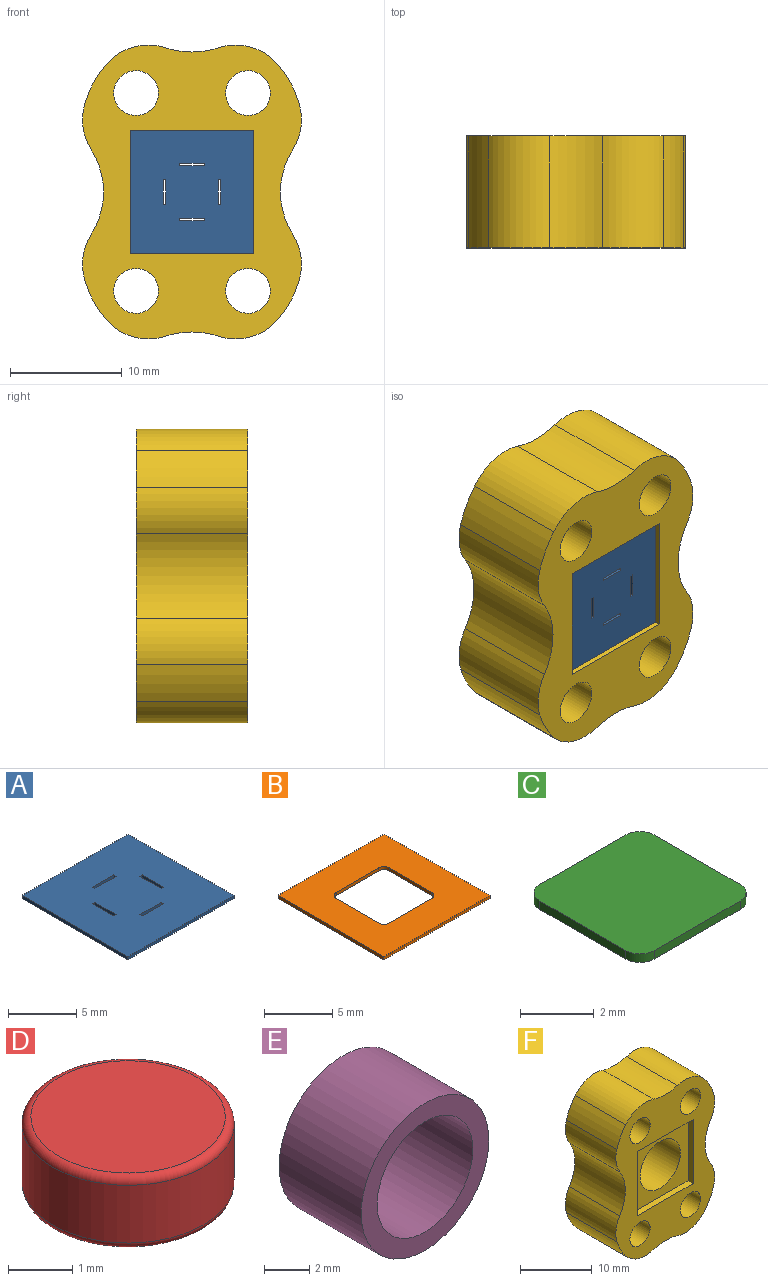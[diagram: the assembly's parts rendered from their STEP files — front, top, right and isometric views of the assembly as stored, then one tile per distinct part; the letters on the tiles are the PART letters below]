
ASSEMBLY  parts=6 mates=13
PART A: 22 faces, bbox 11x11x0.3 mm
  f0: plane 11x11mm, normal (0,0,1), area 118.8mm2, adj f2,f3,f4,f5,f6,f7,f8,f9
  f1: plane 11x11mm, normal (0,0,-1), area 118.8mm2, adj f2,f3,f4,f5,f6,f7,f8,f9
  f2: plane 11x0.28mm, normal (-1,0,0), area 3mm2, adj f0,f1,f3,f5
  f3: plane 11x0.28mm, normal (0,-1,0), area 3mm2, adj f0,f1,f2,f4
  f4: plane 11x0.28mm, normal (1,0,0), area 3mm2, adj f0,f1,f3,f5
  f5: plane 11x0.28mm, normal (0,1,0), area 3mm2, adj f0,f1,f2,f4
  f6: plane 0.28x0.25mm, normal (0,1,0), area 0.1mm2, adj f0,f1,f7,f8
  f7: plane 2.2x0.28mm, normal (1,0,0), area 0.6mm2, adj f0,f1,f6,f9
  f8: plane 2.2x0.28mm, normal (-1,0,0), area 0.6mm2, adj f0,f1,f6,f9
  f9: plane 0.28x0.25mm, normal (0,-1,0), area 0.1mm2, adj f0,f1,f7,f8
  f10: plane 2.2x0.28mm, normal (-1,0,0), area 0.6mm2, adj f0,f1,f11,f12
  f11: plane 0.28x0.25mm, normal (0,1,0), area 0.1mm2, adj f0,f1,f10,f13
  f12: plane 0.28x0.25mm, normal (0,-1,0), area 0.1mm2, adj f0,f1,f10,f13
  f13: plane 2.2x0.28mm, normal (1,0,0), area 0.6mm2, adj f0,f1,f11,f12
  f14: plane 0.28x0.25mm, normal (-1,0,0), area 0.1mm2, adj f0,f1,f15,f17
  f15: plane 2.2x0.28mm, normal (0,-1,0), area 0.6mm2, adj f0,f1,f14,f16
  f16: plane 0.28x0.25mm, normal (1,0,0), area 0.1mm2, adj f0,f1,f15,f17
  f17: plane 2.2x0.28mm, normal (0,1,0), area 0.6mm2, adj f0,f1,f14,f16
  f18: plane 2.2x0.28mm, normal (0,1,0), area 0.6mm2, adj f0,f1,f19,f20
  f19: plane 0.28x0.25mm, normal (1,0,0), area 0.1mm2, adj f0,f1,f18,f21
  f20: plane 0.28x0.25mm, normal (-1,0,0), area 0.1mm2, adj f0,f1,f18,f21
  f21: plane 2.2x0.28mm, normal (0,-1,0), area 0.6mm2, adj f0,f1,f19,f20
PART B: 14 faces, bbox 11x11x0.3 mm
  f0: plane 11x11mm, normal (0,0,-1), area 91mm2, adj f2,f3,f4,f5,f6,f7,f8,f9
  f1: plane 11x11mm, normal (0,0,1), area 91mm2, adj f2,f3,f4,f5,f6,f7,f8,f9
  f2: plane 11x0.28mm, normal (0,1,0), area 3.1mm2, adj f0,f1,f4,f5
  f3: plane 11x0.28mm, normal (0,-1,0), area 3.1mm2, adj f0,f1,f4,f5
  f4: plane 11x0.28mm, normal (1,0,0), area 3.1mm2, adj f0,f1,f2,f3
  f5: plane 11x0.28mm, normal (-1,0,0), area 3.1mm2, adj f0,f1,f2,f3
  f6: cylinder r=0.55mm len=0.55mm, axis (0,0,1), area 0.2mm2, adj f0,f1,f7,f13
  f7: plane 4.4x0.28mm, normal (-1,0,0), area 1.2mm2, adj f0,f1,f6,f8
  f8: cylinder r=0.55mm len=0.55mm, axis (0,0,1), area 0.2mm2, adj f0,f1,f7,f9
  f9: plane 4.4x0.28mm, normal (0,1,0), area 1.2mm2, adj f0,f1,f8,f10
  f10: cylinder r=0.55mm len=0.55mm, axis (0,0,1), area 0.2mm2, adj f0,f1,f9,f11
  f11: plane 4.4x0.28mm, normal (1,0,0), area 1.2mm2, adj f0,f1,f10,f12
  f12: cylinder r=0.55mm len=0.55mm, axis (0,0,1), area 0.2mm2, adj f0,f1,f11,f13
  f13: plane 4.4x0.28mm, normal (0,-1,0), area 1.2mm2, adj f0,f1,f6,f12
PART C: 10 faces, bbox 4.4x4.4x0.3 mm
  f0: plane 4.4x4.4mm, normal (0,0,1), area 19.1mm2, adj f1,f2,f3,f4,f5,f6,f7,f8
  f1: cylinder r=0.55mm len=0.55mm, axis (0,0,1), area 0.2mm2, adj f0,f2,f8,f9
  f2: plane 3.3x0.28mm, normal (-1,0,0), area 0.9mm2, adj f0,f1,f3,f9
  f3: cylinder r=0.55mm len=0.55mm, axis (0,0,1), area 0.2mm2, adj f0,f2,f4,f9
  f4: plane 3.3x0.28mm, normal (0,1,0), area 0.9mm2, adj f0,f3,f5,f9
  f5: cylinder r=0.55mm len=0.55mm, axis (0,0,1), area 0.2mm2, adj f0,f4,f6,f9
  f6: plane 3.3x0.28mm, normal (1,0,0), area 0.9mm2, adj f0,f5,f7,f9
  f7: cylinder r=0.55mm len=0.55mm, axis (0,0,1), area 0.2mm2, adj f0,f6,f8,f9
  f8: plane 3.3x0.28mm, normal (0,-1,0), area 0.9mm2, adj f0,f1,f7,f9
  f9: plane 4.4x4.4mm, normal (0,0,-1), area 19.1mm2, adj f1,f2,f3,f4,f5,f6,f7,f8
PART D: 5 faces, bbox 3.6x3.6x1.4 mm
  f0: cylinder r=1.65mm len=3.3mm, axis (0,0,-1), area 11.4mm2, adj f3,f4
  f1: plane 3.03x3.03mm, normal (0,0,1), area 7.2mm2, adj f4
  f2: plane 3.03x3.03mm, normal (0,0,-1), area 7.2mm2, adj f3
  f3: torus R=1.51mm, axis (0,0,1), area 2.2mm2, adj f0,f2
  f4: torus R=1.51mm, axis (0,0,1), area 2.2mm2, adj f0,f1
PART E: 4 faces, bbox 8x5.2x8 mm
  f0: cylinder r=3mm len=6mm, axis (0,1,0), area 97.1mm2, adj f2,f3
  f1: cylinder r=4mm len=8mm, axis (0,1,0), area 129.4mm2, adj f2,f3
  f2: plane 8x8mm, normal (0,-1,0), area 22mm2, adj f0,f1
  f3: plane 8x8mm, normal (0,1,0), area 22mm2, adj f0,f1
PART F: 30 faces, bbox 19.6x10x26.3 mm
  f0: plane 26.25x19.57mm, normal (0,-1,0), area 274.4mm2, adj f3,f4,f6,f7,f8,f9,f11,f12
  f1: cylinder r=4mm len=8mm, axis (0,-1,0), area 201.1mm2, adj f10,f25
  f2: plane 26.25x19.57mm, normal (0,1,0), area 367.1mm2, adj f3,f4,f5,f6,f7,f8,f9,f11
  f3: cylinder r=10mm len=10mm, axis (0,-1,0), area 38mm2, adj f0,f2,f20,f22
  f4: cylinder r=10mm len=10mm, axis (0,1,0), area 38mm2, adj f0,f2,f17,f24
  f5: cylinder r=3mm len=6mm, axis (0,1,0), area 18.8mm2, adj f2,f10
  f6: cylinder r=2mm len=10mm, axis (0,1,0), area 125.7mm2, adj f0,f2
  f7: cylinder r=2mm len=10mm, axis (0,1,0), area 125.7mm2, adj f0,f2
  f8: cylinder r=2mm len=10mm, axis (0,1,0), area 125.7mm2, adj f0,f2
  f9: cylinder r=2mm len=10mm, axis (0,1,0), area 125.7mm2, adj f0,f2
  f10: plane 8x8mm, normal (0,-1,0), area 22mm2, adj f1,f5
  f11: cylinder r=10mm len=10mm, axis (0,-1,0), area 38mm2, adj f0,f2,f19,f23
  f12: cylinder r=10mm len=10mm, axis (0,1,0), area 38mm2, adj f0,f2,f18,f21
  f13: cylinder r=7.5mm len=10mm, axis (0,-1,0), area 47.6mm2, adj f0,f2,f17,f18
  f14: cylinder r=7.5mm len=10mm, axis (0,-1,0), area 47.6mm2, adj f0,f2,f19,f20
  f15: cylinder r=7mm len=10mm, axis (0,-1,0), area 79.5mm2, adj f0,f2,f23,f24
  f16: cylinder r=7mm len=10mm, axis (0,-1,0), area 79.5mm2, adj f0,f2,f21,f22
  f17: cylinder r=5mm len=10mm, axis (0,-1,0), area 60.7mm2, adj f0,f2,f4,f13
  f18: cylinder r=5mm len=10mm, axis (0,1,0), area 60.7mm2, adj f0,f2,f12,f13
  f19: cylinder r=5mm len=10mm, axis (0,1,0), area 60.7mm2, adj f0,f2,f11,f14
  f20: cylinder r=5mm len=10mm, axis (0,1,0), area 60.7mm2, adj f0,f2,f3,f14
  f21: cylinder r=5mm len=10mm, axis (0,-1,0), area 43.2mm2, adj f0,f2,f12,f16
  f22: cylinder r=5mm len=10mm, axis (0,1,0), area 43.2mm2, adj f0,f2,f3,f16
  f23: cylinder r=5mm len=10mm, axis (0,-1,0), area 43.2mm2, adj f0,f2,f11,f15
  f24: cylinder r=5mm len=10mm, axis (0,1,0), area 43.2mm2, adj f0,f2,f4,f15
  f25: plane 11x11mm, normal (0,-1,0), area 70.7mm2, adj f1,f26,f27,f28,f29
  f26: plane 11x1mm, normal (0,0,-1), area 11mm2, adj f0,f25,f27,f29
  f27: plane 11x1mm, normal (1,0,0), area 11mm2, adj f0,f25,f26,f28
  f28: plane 11x1mm, normal (0,0,1), area 11mm2, adj f0,f25,f27,f29
  f29: plane 11x1mm, normal (-1,0,0), area 11mm2, adj f0,f25,f26,f28
PLACE A rot(axis=(-0.58,0.58,0.58),120deg) t=(-5.5,88.11,5.5)mm
PLACE B rot(axis=(-0.58,0.58,0.58),120deg) t=(-5.5,88.11,5.5)mm
PLACE C rot(axis=(-0.58,-0.58,-0.58),120deg) t=(5.5,88.11,-5.5)mm
PLACE D rot(axis=(-0.86,0.36,0.36),98.8deg) t=(-7.78,88.11,0.15)mm
PLACE E rot(axis=(0,-1,0),180deg) t=(0,97.12,0)mm
PLACE F rot(axis=(0,1,0),180deg) t=(-40.26,98.12,21.8)mm
MATE cylindrical B.f1 <-> A.f0  axis (0,1,0) through (0,89.12,0)mm
MATE cylindrical D.f0 <-> F.f1  axis (0,1,0) through (0,90.5,0)mm
MATE cylindrical D.f0 <-> C.f0  axis (0,1,0) through (0,90.5,0)mm
MATE planar F.f25 <-> B.f1  axis (0,-1,0) through (-5.5,89.12,0)mm
MATE planar E.f0 <-> F.f1  axis (0,1,0) through (0,97.12,0)mm
MATE planar A.f0 <-> C.f9  axis (0,1,0) through (0,88.84,0)mm
MATE planar A.f0 <-> B.f0  axis (0,1,0) through (0,88.84,0)mm
MATE planar A.f4 <-> B.f4  axis (0,0,-1) through (0,88.71,-5.5)mm
MATE cylindrical A.f0 <-> C.f9  axis (0,1,0) through (0,88.84,0)mm
MATE cylindrical E.f0 <-> F.f1  axis (0,-1,0) through (0,91.97,0)mm
MATE planar B.f2 <-> F.f29  axis (-1,0,0) through (-5.5,88.98,0)mm
MATE planar D.f0 <-> C.f0  axis (0,-1,0) through (0,89.12,0)mm
MATE cylindrical C.f8 <-> B.f13  axis (-1,0,0) through (-2.2,88.98,0)mm
